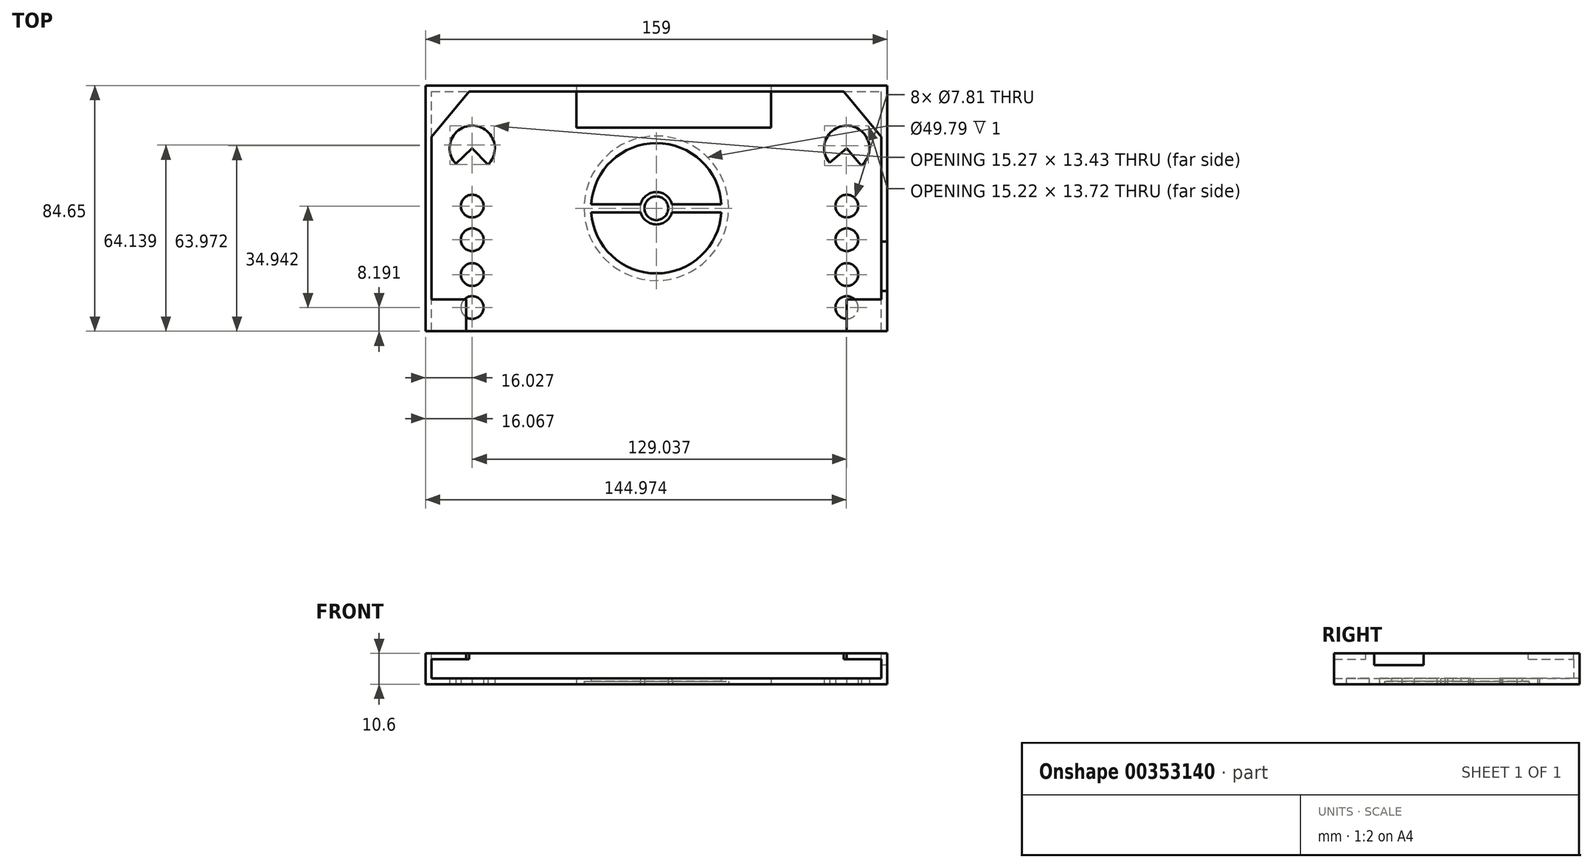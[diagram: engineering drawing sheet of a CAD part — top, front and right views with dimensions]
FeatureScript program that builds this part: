
annotation { "Feature Type Name" : "Feature", "Feature Type Description" : "" }
export const myFeature = defineFeature(function(context is Context, id is Id, definition is map)
    precondition{}
    {
        {
            var Q0;
            Q0=qCreatedBy(makeId("Top.planeOp"),FACE);
            var sketch = newSketch(context, id + "F0", { "sketchPlane" : qUnion([Q0])});
            skLineSegment(sketch, "E0.bottom", {"start": v(-37.9, -14.46) * mm, "end": v(117.1, -14.46) * mm});
            skLineSegment(sketch, "E0.top", {"start": v(-37.9, 66.2) * mm, "end": v(117.1, 66.2) * mm});
            skLineSegment(sketch, "E0.left", {"start": v(-37.9, -14.46) * mm, "end": v(-37.9, 66.2) * mm});
            skLineSegment(sketch, "E0.right", {"start": v(117.1, -14.46) * mm, "end": v(117.1, 66.2) * mm});
            skSolve(sketch);
        }
        {
            var Q0;
            Q0=makeQuery(id+"F0.imprint","IMPRINT",FACE,{"disambiguationData":[TD([[makeQuery(id+"F0.imprint","IMPRINT",EDGE,{"derivedFrom":sQuery(id+"F0.wireOp",EDGE,"E0.bottom")}),1.0]])]});
            extrude(context, id + "F1", {"entities" : qUnion([Q0]), "depth" : 6.6 * mm});
        }
        {
            var Q0;
            Q0=makeQuery(id+"F1.opExtrude","CAP_FACE",FACE,{"disambiguationData":[OSD([sQuery(id+"F0.wireOp",EDGE,"E0.bottom"),sQuery(id+"F0.wireOp",EDGE,"E0.top"),sQuery(id+"F0.wireOp",EDGE,"E0.left"),sQuery(id+"F0.wireOp",EDGE,"E0.right")])],"isStart":false});
            var Q1;
            Q1=makeQuery(id+"F1.opExtrude","SWEPT_BODY",BODY,{"disambiguationData":[OSD([sQuery(id+"F0.wireOp",EDGE,"E0.bottom"),sQuery(id+"F0.wireOp",EDGE,"E0.top"),sQuery(id+"F0.wireOp",EDGE,"E0.left"),sQuery(id+"F0.wireOp",EDGE,"E0.right")])]});
            shell(context, id + "F2", {"isHollow" : true, "entities" : qUnion([Q0]), "parts" : qUnion([Q1]), "thickness" : 2 * mm, "oppositeDirection" : true});
        }
        {
            var Q0;
            Q0=makeQuery(id+"F1.opExtrude","CAP_FACE",FACE,{"disambiguationData":[OSD([sQuery(id+"F0.wireOp",EDGE,"E0.bottom"),sQuery(id+"F0.wireOp",EDGE,"E0.top"),sQuery(id+"F0.wireOp",EDGE,"E0.left"),sQuery(id+"F0.wireOp",EDGE,"E0.right")])],"isStart":false});
            var sketch = newSketch(context, id + "F3", { "sketchPlane" : qUnion([Q0])});
            skLineSegment(sketch, "E1", {"start": v(-37.9, -16.46) * mm, "end": v(-37.9, 66.2) * mm});
            skLineSegment(sketch, "E2", {"start": v(-37.9, 66.2) * mm, "end": v(117.1, 66.2) * mm});
            skLineSegment(sketch, "E3", {"start": v(117.1, 66.2) * mm, "end": v(117.1, -16.46) * mm});
            skLineSegment(sketch, "E4", {"start": v(-37.9, 50.52) * mm, "end": v(-24.9, 66.2) * mm});
            skLineSegment(sketch, "E5", {"start": v(104.1, 66.2) * mm, "end": v(117.1, 50.52) * mm});
            skLineSegment(sketch, "E6", {"start": v(110.6, 58.36) * mm, "end": v(119.1, 68.2) * mm});
            skLineSegment(sketch, "E7", {"start": v(-31.4, 58.36) * mm, "end": v(-39.9, 68.2) * mm});
            skLineSegment(sketch, "E8.bottom", {"start": v(-37.9, -16.46) * mm, "end": v(-25.9, -16.46) * mm});
            skLineSegment(sketch, "E8.top", {"start": v(-37.9, -5.46) * mm, "end": v(-25.9, -5.46) * mm});
            skLineSegment(sketch, "E8.left", {"start": v(-37.9, -16.46) * mm, "end": v(-37.9, -5.46) * mm});
            skLineSegment(sketch, "E8.right", {"start": v(-25.9, -16.46) * mm, "end": v(-25.9, -5.46) * mm});
            skLineSegment(sketch, "E9.bottom", {"start": v(117.1, -16.46) * mm, "end": v(105.1, -16.46) * mm});
            skLineSegment(sketch, "E9.top", {"start": v(117.1, -5.46) * mm, "end": v(105.1, -5.46) * mm});
            skLineSegment(sketch, "E9.left", {"start": v(117.1, -16.46) * mm, "end": v(117.1, -5.46) * mm});
            skLineSegment(sketch, "E9.right", {"start": v(105.1, -16.46) * mm, "end": v(105.1, -5.46) * mm});
            skSolve(sketch);
        }
        {
            var Q0;
            {var subQ0=sQuery(id+"F3.wireOp",EDGE,"E8.top");Q0=makeQuery(id+"F3.imprint","IMPRINT",FACE,{"disambiguationData":[TD([[makeQuery(id+"F3.imprint","IMPRINT",EDGE,{"derivedFrom":subQ0}),1.0]])]});}
            extrude(context, id + "F4", {"entities" : qUnion([Q0]), "operationType" : NewBodyOperationType.REMOVE, "oppositeDirection" : true, "depth" : 4.4 * mm});
        }
        {
            var Q0;
            Q0=makeQuery(id+"F2.opShell","OFFSET_FACE",FACE,{"disambiguationData":[OSD([sQuery(id+"F0.wireOp",EDGE,"E0.bottom")])]});
            var sketch = newSketch(context, id + "F5", { "sketchPlane" : qUnion([Q0])});
            skLineSegment(sketch, "E10.bottom", {"start": v(37.9, 0) * mm, "end": v(-117.1, 0) * mm});
            skLineSegment(sketch, "E10.top", {"start": v(37.9, 6.6) * mm, "end": v(-117.1, 6.6) * mm});
            skLineSegment(sketch, "E10.left", {"start": v(37.9, 0) * mm, "end": v(37.9, 6.6) * mm});
            skLineSegment(sketch, "E10.right", {"start": v(-117.1, 0) * mm, "end": v(-117.1, 6.6) * mm});
            skSolve(sketch);
        }
        {
            var Q0;
            Q0=makeQuery(id+"F5.imprint","IMPRINT",FACE,{"disambiguationData":[TD([[makeQuery(id+"F5.imprint","IMPRINT",EDGE,{"derivedFrom":sQuery(id+"F5.wireOp",EDGE,"E10.bottom")}),-1.0]])]});
            extrude(context, id + "F6", {"entities" : qUnion([Q0]), "operationType" : NewBodyOperationType.REMOVE, "oppositeDirection" : true, "depth" : 25 * mm});
        }
        {
            var Q0;
            Q0=makeQuery(id+"F1.opExtrude","CAP_FACE",FACE,{"disambiguationData":[OSD([sQuery(id+"F0.wireOp",EDGE,"E0.bottom"),sQuery(id+"F0.wireOp",EDGE,"E0.top"),sQuery(id+"F0.wireOp",EDGE,"E0.left"),sQuery(id+"F0.wireOp",EDGE,"E0.right")])],"isStart":false});
            var sketch = newSketch(context, id + "F7", { "sketchPlane" : qUnion([Q0])});
            skLineSegment(sketch, "E11", {"start": v(119.1, -16.46) * mm, "end": v(119.1, -2.56) * mm});
            skLineSegment(sketch, "E12.bottom", {"start": v(119.1, -2.56) * mm, "end": v(117.1, -2.56) * mm});
            skLineSegment(sketch, "E12.top", {"start": v(119.1, 14.5) * mm, "end": v(117.1, 14.5) * mm});
            skLineSegment(sketch, "E12.left", {"start": v(119.1, -2.56) * mm, "end": v(119.1, 14.5) * mm});
            skLineSegment(sketch, "E12.right", {"start": v(117.1, -2.56) * mm, "end": v(117.1, 14.5) * mm});
            skSolve(sketch);
        }
        {
            var Q0;
            Q0=makeQuery(id+"F7.imprint","IMPRINT",FACE,{"disambiguationData":[TD([[makeQuery(id+"F7.imprint","IMPRINT",EDGE,{"derivedFrom":sQuery(id+"F7.wireOp",EDGE,"E12.bottom")}),-1.0]])]});
            extrude(context, id + "F8", {"entities" : qUnion([Q0]), "operationType" : NewBodyOperationType.REMOVE, "oppositeDirection" : true, "depth" : 4 * mm});
        }
        {
            var Q0;
            Q0=makeQuery(id+"F1.opExtrude","CAP_FACE",FACE,{"disambiguationData":[OSD([sQuery(id+"F0.wireOp",EDGE,"E0.bottom"),sQuery(id+"F0.wireOp",EDGE,"E0.top"),sQuery(id+"F0.wireOp",EDGE,"E0.left"),sQuery(id+"F0.wireOp",EDGE,"E0.right")])],"isStart":true});
            var sketch = newSketch(context, id + "F9", { "sketchPlane" : qUnion([Q0])});
            skLineSegment(sketch, "E13.bottom", {"start": v(79.1, -68.2) * mm, "end": v(12.1, -68.2) * mm});
            skLineSegment(sketch, "E13.top", {"start": v(79.1, -53.65) * mm, "end": v(12.1, -53.65) * mm});
            skLineSegment(sketch, "E13.left", {"start": v(79.1, -68.2) * mm, "end": v(79.1, -53.65) * mm});
            skLineSegment(sketch, "E13.right", {"start": v(12.1, -68.2) * mm, "end": v(12.1, -53.65) * mm});
            skSolve(sketch);
        }
        {
            var Q0;
            Q0=makeQuery(id+"F9.imprint","IMPRINT",FACE,{"disambiguationData":[TD([[makeQuery(id+"F9.imprint","IMPRINT",EDGE,{"derivedFrom":sQuery(id+"F9.wireOp",EDGE,"E13.bottom")}),1.0]])]});
            extrude(context, id + "F10", {"entities" : qUnion([Q0]), "operationType" : NewBodyOperationType.REMOVE, "oppositeDirection" : true, "depth" : 2 * mm});
        }
        {
            var Q0;
            Q0=makeQuery(id+"F1.opExtrude","CAP_FACE",FACE,{"disambiguationData":[OSD([sQuery(id+"F0.wireOp",EDGE,"E0.bottom"),sQuery(id+"F0.wireOp",EDGE,"E0.top"),sQuery(id+"F0.wireOp",EDGE,"E0.left"),sQuery(id+"F0.wireOp",EDGE,"E0.right")])],"isStart":true});
            var sketch = newSketch(context, id + "F11", { "sketchPlane" : qUnion([Q0])});
            skLineSegment(sketch, "E14", {"start": v(39.6, 16.46) * mm, "end": v(39.6, -68.33) * mm});
            skCircle(sketch, "E15", {"center": v(39.6, -25.93) * mm, "radius": 24.9 * mm});
            skCircle(sketch, "E16", {"center": v(39.6, -25.93) * mm, "radius": 22.46 * mm});
            skCircle(sketch, "E17", {"center": v(39.6, -25.93) * mm, "radius": 4.08 * mm});
            skCircle(sketch, "E18", {"center": v(39.6, -25.93) * mm, "radius": 5.57 * mm});
            skLineSegment(sketch, "E19", {"start": v(17.18, -27.32) * mm, "end": v(34.2, -27.32) * mm});
            skLineSegment(sketch, "E20", {"start": v(45, -27.32) * mm, "end": v(62.01, -27.32) * mm});
            skLineSegment(sketch, "E21", {"start": v(17.19, -24.53) * mm, "end": v(34.2, -24.53) * mm});
            skLineSegment(sketch, "E22", {"start": v(45, -24.53) * mm, "end": v(62.01, -24.53) * mm});
            skCircle(sketch, "E23", {"center": v(-23.83, -46.61) * mm, "radius": 7.79 * mm});
            skLineSegment(sketch, "E24", {"start": v(-23.83, -46.61) * mm, "end": v(-29.48, -41.25) * mm});
            skLineSegment(sketch, "E25", {"start": v(-23.83, -46.61) * mm, "end": v(-18.47, -40.96) * mm});
            skCircle(sketch, "E26", {"center": v(-23.83, -26.67) * mm, "radius": 3.9 * mm});
            skCircle(sketch, "E27", {"center": v(-23.83, -15.08) * mm, "radius": 3.9 * mm});
            skCircle(sketch, "E28", {"center": v(-23.83, -3.09) * mm, "radius": 3.9 * mm});
            skCircle(sketch, "E29", {"center": v(-23.83, 8.27) * mm, "radius": 3.9 * mm});
            skCircle(sketch, "E30", {"center": v(105.2, -46.61) * mm, "radius": 7.79 * mm});
            skLineSegment(sketch, "E31", {"start": v(105.2, -46.61) * mm, "end": v(99.25, -41.6) * mm});
            skLineSegment(sketch, "E32", {"start": v(105.2, -46.61) * mm, "end": v(110.22, -40.65) * mm});
            skCircle(sketch, "E33", {"center": v(105.2, -26.67) * mm, "radius": 3.9 * mm});
            skCircle(sketch, "E34", {"center": v(105.2, -15.08) * mm, "radius": 3.9 * mm});
            skCircle(sketch, "E35", {"center": v(105.2, -3.09) * mm, "radius": 3.9 * mm});
            skCircle(sketch, "E36", {"center": v(105.2, 8.27) * mm, "radius": 3.9 * mm});
            skSolve(sketch);
        }
        {
            var Q0;
            {var subQ0=sQuery(id+"F11.wireOp",EDGE,"E24");Q0=makeQuery(id+"F11.imprint","IMPRINT",FACE,{"disambiguationData":[TD([[makeQuery(id+"F11.imprint","IMPRINT",EDGE,{"derivedFrom":subQ0}),1.0]])]});}
            var Q1;
            Q1=makeQuery(id+"F11.imprint","IMPRINT",FACE,{"disambiguationData":[TD([[makeQuery(id+"F11.imprint","IMPRINT",EDGE,{"derivedFrom":sQuery(id+"F11.wireOp",EDGE,"E26")}),1.0]])]});
            var Q2;
            Q2=makeQuery(id+"F11.imprint","IMPRINT",FACE,{"disambiguationData":[TD([[makeQuery(id+"F11.imprint","IMPRINT",EDGE,{"derivedFrom":sQuery(id+"F11.wireOp",EDGE,"E27")}),1.0]])]});
            var Q3;
            Q3=makeQuery(id+"F11.imprint","IMPRINT",FACE,{"disambiguationData":[TD([[makeQuery(id+"F11.imprint","IMPRINT",EDGE,{"derivedFrom":sQuery(id+"F11.wireOp",EDGE,"E28")}),1.0]])]});
            var Q4;
            Q4=makeQuery(id+"F11.imprint","IMPRINT",FACE,{"disambiguationData":[TD([[makeQuery(id+"F11.imprint","IMPRINT",EDGE,{"derivedFrom":sQuery(id+"F11.wireOp",EDGE,"E29")}),1.0]])]});
            var Q5;
            Q5=makeQuery(id+"F11.imprint","IMPRINT",FACE,{"disambiguationData":[TD([[makeQuery(id+"F11.imprint","IMPRINT",EDGE,{"derivedFrom":sQuery(id+"F11.wireOp",EDGE,"E35")}),1.0]])]});
            var Q6;
            Q6=makeQuery(id+"F11.imprint","IMPRINT",FACE,{"disambiguationData":[TD([[makeQuery(id+"F11.imprint","IMPRINT",EDGE,{"derivedFrom":sQuery(id+"F11.wireOp",EDGE,"E34")}),1.0]])]});
            var Q7;
            Q7=makeQuery(id+"F11.imprint","IMPRINT",FACE,{"disambiguationData":[TD([[makeQuery(id+"F11.imprint","IMPRINT",EDGE,{"derivedFrom":sQuery(id+"F11.wireOp",EDGE,"E33")}),1.0]])]});
            var Q8;
            {var subQ0=sQuery(id+"F11.wireOp",EDGE,"E31");Q8=makeQuery(id+"F11.imprint","IMPRINT",FACE,{"disambiguationData":[TD([[makeQuery(id+"F11.imprint","IMPRINT",EDGE,{"derivedFrom":subQ0}),1.0]])]});}
            var Q9;
            Q9=makeQuery(id+"F11.imprint","IMPRINT",FACE,{"disambiguationData":[TD([[makeQuery(id+"F11.imprint","IMPRINT",EDGE,{"derivedFrom":sQuery(id+"F11.wireOp",EDGE,"E36")}),1.0]])]});
            var Q10;
            {var subQ5=sQuery(id+"F11.wireOp",EDGE,"E19");Q10=makeQuery(id+"F11.imprint","IMPRINT",FACE,{"disambiguationData":[TD([[makeQuery(id+"F11.imprint","IMPRINT",EDGE,{"derivedFrom":subQ5}),-1.0]])]});}
            var Q11;
            {var subQ5=sQuery(id+"F11.wireOp",EDGE,"E20");Q11=makeQuery(id+"F11.imprint","IMPRINT",FACE,{"disambiguationData":[TD([[makeQuery(id+"F11.imprint","IMPRINT",EDGE,{"derivedFrom":subQ5}),-1.0]])]});}
            var Q12;
            {var subQ5=sQuery(id+"F11.wireOp",EDGE,"E22");Q12=makeQuery(id+"F11.imprint","IMPRINT",FACE,{"disambiguationData":[TD([[makeQuery(id+"F11.imprint","IMPRINT",EDGE,{"derivedFrom":subQ5}),1.0]])]});}
            var Q13;
            {var subQ5=sQuery(id+"F11.wireOp",EDGE,"E21");Q13=makeQuery(id+"F11.imprint","IMPRINT",FACE,{"disambiguationData":[TD([[makeQuery(id+"F11.imprint","IMPRINT",EDGE,{"derivedFrom":subQ5}),1.0]])]});}
            var Q14;
            {var subQ0=sQuery(id+"F11.wireOp",EDGE,"E17");var subQ1=sQuery(id+"F11.wireOp",EDGE,"E14");var subQ2=makeQuery(id+"F11.imprint","INTERSECT",VERTEX,{"disambiguationData":[OD(0.0)],"derivedFrom":[subQ1,subQ0]});Q14=makeQuery(id+"F11.imprint","IMPRINT",FACE,{"disambiguationData":[TD([[makeQuery(id+"F11.imprint","IMPRINT",EDGE,{"disambiguationData":[TD([[subQ2,-1.0]])],"derivedFrom":subQ1}),-1.0]])]});}
            var Q15;
            {var subQ0=sQuery(id+"F11.wireOp",EDGE,"E17");var subQ1=sQuery(id+"F11.wireOp",EDGE,"E14");var subQ2=makeQuery(id+"F11.imprint","INTERSECT",VERTEX,{"disambiguationData":[OD(0.0)],"derivedFrom":[subQ1,subQ0]});Q15=makeQuery(id+"F11.imprint","IMPRINT",FACE,{"disambiguationData":[TD([[makeQuery(id+"F11.imprint","IMPRINT",EDGE,{"disambiguationData":[TD([[subQ2,-1.0]])],"derivedFrom":subQ1}),1.0]])]});}
            extrude(context, id + "F12", {"entities" : qUnion([Q0, Q1, Q2, Q3, Q4, Q5, Q6, Q7, Q8, Q9, Q10, Q11, Q12, Q13, Q14, Q15]), "operationType" : NewBodyOperationType.REMOVE, "oppositeDirection" : true, "depth" : 2 * mm});
        }
        {
            var Q0;
            {var subQ0=sQuery(id+"F11.wireOp",EDGE,"E15");var subQ1=sQuery(id+"F11.wireOp",EDGE,"E14");var subQ2=makeQuery(id+"F11.imprint","INTERSECT",VERTEX,{"disambiguationData":[OD(0.0)],"derivedFrom":[subQ1,subQ0]});Q0=makeQuery(id+"F11.imprint","IMPRINT",FACE,{"disambiguationData":[TD([[makeQuery(id+"F11.imprint","IMPRINT",EDGE,{"disambiguationData":[TD([[subQ2,-1.0]])],"derivedFrom":subQ1}),-1.0]])]});}
            var Q1;
            {var subQ0=sQuery(id+"F11.wireOp",EDGE,"E15");var subQ1=sQuery(id+"F11.wireOp",EDGE,"E14");var subQ2=makeQuery(id+"F11.imprint","INTERSECT",VERTEX,{"disambiguationData":[OD(0.0)],"derivedFrom":[subQ1,subQ0]});Q1=makeQuery(id+"F11.imprint","IMPRINT",FACE,{"disambiguationData":[TD([[makeQuery(id+"F11.imprint","IMPRINT",EDGE,{"disambiguationData":[TD([[subQ2,-1.0]])],"derivedFrom":subQ1}),1.0]])]});}
            var Q2;
            {var subQ0=sQuery(id+"F11.wireOp",EDGE,"E20");Q2=makeQuery(id+"F11.imprint","IMPRINT",FACE,{"disambiguationData":[TD([[makeQuery(id+"F11.imprint","IMPRINT",EDGE,{"derivedFrom":subQ0}),1.0]])]});}
            var Q3;
            {var subQ0=sQuery(id+"F11.wireOp",EDGE,"E18");var subQ2=sQuery(id+"F11.wireOp",EDGE,"E14");var subQ3=makeQuery(id+"F11.imprint","INTERSECT",VERTEX,{"disambiguationData":[OD(0.0)],"derivedFrom":[subQ2,subQ0]});Q3=makeQuery(id+"F11.imprint","IMPRINT",FACE,{"disambiguationData":[TD([[makeQuery(id+"F11.imprint","IMPRINT",EDGE,{"disambiguationData":[TD([[subQ3,-1.0]])],"derivedFrom":subQ2}),1.0]])]});}
            var Q4;
            {var subQ1=sQuery(id+"F11.wireOp",EDGE,"E14");var subQ4=sQuery(id+"F11.wireOp",EDGE,"E18");var subQ6=makeQuery(id+"F11.imprint","INTERSECT",VERTEX,{"disambiguationData":[OD(0.0)],"derivedFrom":[subQ1,subQ4]});Q4=makeQuery(id+"F11.imprint","IMPRINT",FACE,{"disambiguationData":[TD([[makeQuery(id+"F11.imprint","IMPRINT",EDGE,{"disambiguationData":[TD([[subQ6,-1.0]])],"derivedFrom":subQ1}),-1.0]])]});}
            var Q5;
            {var subQ0=sQuery(id+"F11.wireOp",EDGE,"E19");Q5=makeQuery(id+"F11.imprint","IMPRINT",FACE,{"disambiguationData":[TD([[makeQuery(id+"F11.imprint","IMPRINT",EDGE,{"derivedFrom":subQ0}),1.0]])]});}
            extrude(context, id + "F13", {"entities" : qUnion([Q0, Q1, Q2, Q3, Q4, Q5]), "operationType" : NewBodyOperationType.REMOVE, "oppositeDirection" : true, "depth" : 1 * mm});
        }
    });
